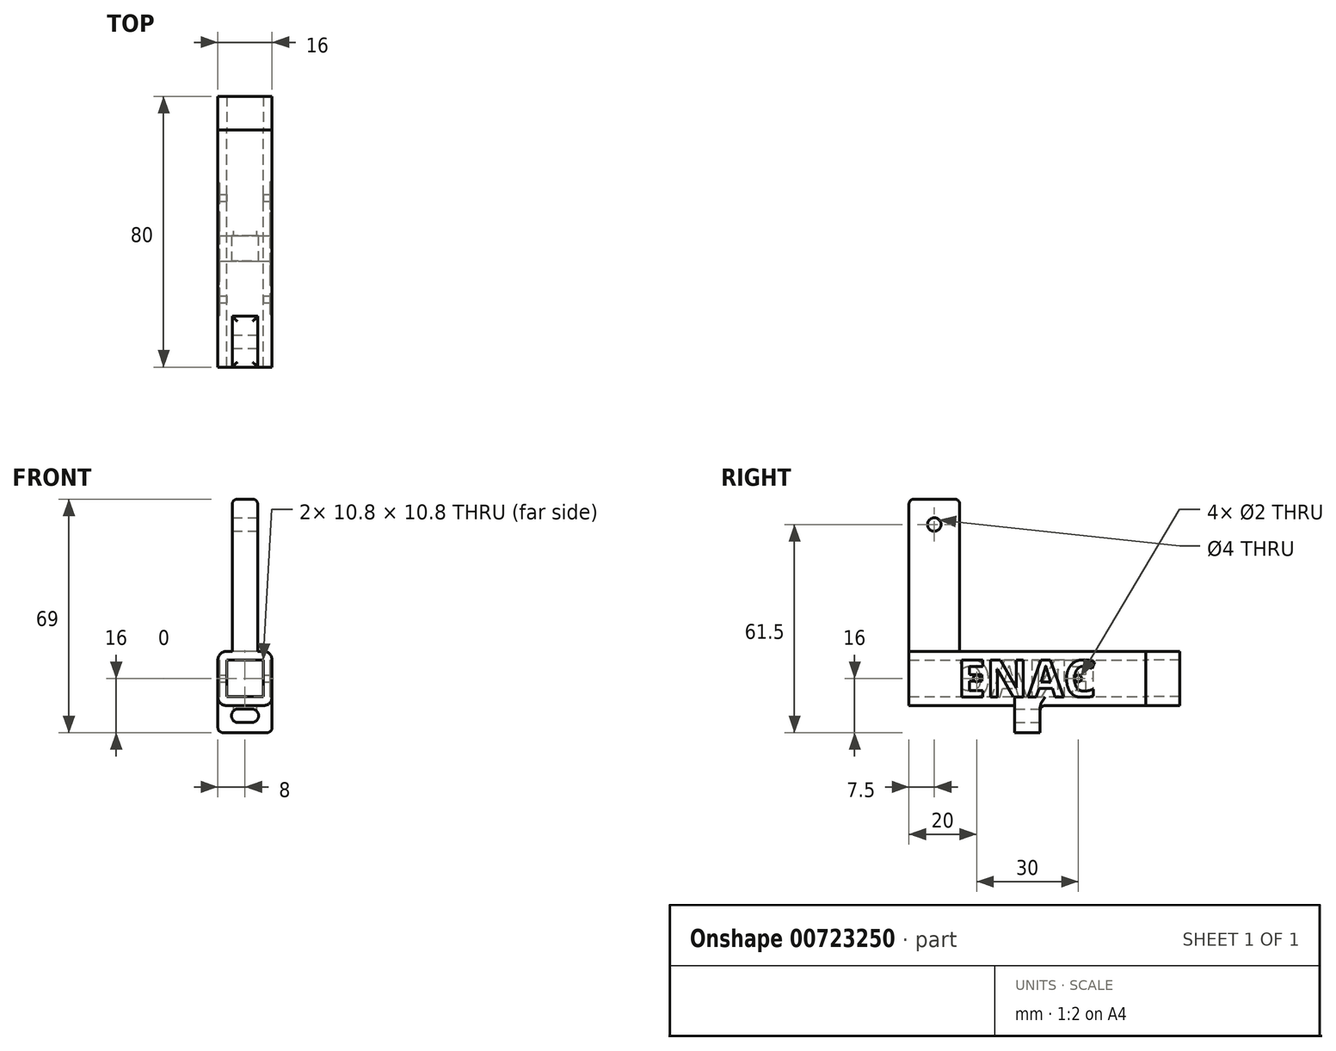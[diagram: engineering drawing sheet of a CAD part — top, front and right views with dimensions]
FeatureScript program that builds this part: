
annotation { "Feature Type Name" : "Feature", "Feature Type Description" : "" }
export const myFeature = defineFeature(function(context is Context, id is Id, definition is map)
    precondition{}
    {
        {
            var Q0;
            Q0=qCreatedBy(makeId("Front.planeOp"),FACE);
            var sketch = newSketch(context, id + "F0", { "sketchPlane" : qUnion([Q0]), "asVersion" : FeatureScriptVersionNumber.V686_LOFT_FS_BUG_FIXES});
            skLineSegment(sketch, "E0.bottom", {"start": v(8, 8) * mm, "end": v(-8, 8) * mm});
            skLineSegment(sketch, "E0.top", {"start": v(8, -8) * mm, "end": v(-8, -8) * mm});
            skLineSegment(sketch, "E0.left", {"start": v(8, 8) * mm, "end": v(8, -8) * mm});
            skLineSegment(sketch, "E0.right", {"start": v(-8, 8) * mm, "end": v(-8, -8) * mm});
            skPoint(sketch, "E0.middle", {"position": v(0, 0) * mm});
            skLineSegment(sketch, "E1.0", {"start": v(5.4, 5.4) * mm, "end": v(-5.4, 5.4) * mm});
            skLineSegment(sketch, "E1.1", {"start": v(5.4, 5.4) * mm, "end": v(5.4, -5.4) * mm});
            skLineSegment(sketch, "E1.2", {"start": v(5.4, -5.4) * mm, "end": v(-5.4, -5.4) * mm});
            skLineSegment(sketch, "E1.3", {"start": v(-5.4, 5.4) * mm, "end": v(-5.4, -5.4) * mm});
            skLineSegment(sketch, "E2.bottom", {"start": v(-8, -8) * mm, "end": v(8, -8) * mm});
            skLineSegment(sketch, "E2.top", {"start": v(-8, -16) * mm, "end": v(8, -16) * mm});
            skLineSegment(sketch, "E2.left", {"start": v(-8, -8) * mm, "end": v(-8, -16) * mm});
            skLineSegment(sketch, "E2.right", {"start": v(8, -8) * mm, "end": v(8, -16) * mm});
            skLineSegment(sketch, "E3", {"start": v(0, -8) * mm, "end": v(0, -16) * mm});
            skLineSegment(sketch, "E4.bottom", {"start": v(4, -9) * mm, "end": v(-4, -9) * mm});
            skLineSegment(sketch, "E4.top", {"start": v(4, -13) * mm, "end": v(-4, -13) * mm});
            skLineSegment(sketch, "E4.left", {"start": v(4, -9) * mm, "end": v(4, -13) * mm});
            skLineSegment(sketch, "E4.right", {"start": v(-4, -9) * mm, "end": v(-4, -13) * mm});
            skPoint(sketch, "E4.middle", {"position": v(0, -11) * mm});
            skSolve(sketch);
        }
        {
            var Q0;
            Q0=makeQuery(id+"F0.imprint","IMPRINT",FACE,{"disambiguationData":[TD([[makeQuery(id+"F0.imprint","IMPRINT",EDGE,{"derivedFrom":sQuery(id+"F0.wireOp",EDGE,"E0.bottom")}),1.0]])]});
            extrude(context, id + "F1", {"entities" : qUnion([Q0]), "endBound" : BoundingType.SYMMETRIC, "depth" : 70 * mm, "offsetDistance" : 25 * mm});
        }
        {
            var Q0;
            {var subQ5=sQuery(id+"F0.wireOp",EDGE,"E2.left");Q0=makeQuery(id+"F0.imprint","IMPRINT",FACE,{"disambiguationData":[TD([[makeQuery(id+"F0.imprint","IMPRINT",EDGE,{"derivedFrom":subQ5}),1.0]])]});}
            var Q1;
            {var subQ0=sQuery(id+"F0.wireOp",EDGE,"E2.right");Q1=makeQuery(id+"F0.imprint","IMPRINT",FACE,{"disambiguationData":[TD([[makeQuery(id+"F0.imprint","IMPRINT",EDGE,{"derivedFrom":subQ0}),-1.0]])]});}
            extrude(context, id + "F2", {"entities" : qUnion([Q0, Q1]), "operationType" : NewBodyOperationType.ADD, "endBound" : BoundingType.SYMMETRIC, "depth" : 7.5 * mm, "offsetDistance" : 25 * mm});
        }
        {
            var Q0;
            Q0=qCreatedBy(makeId("Right.planeOp"),FACE);
            var sketch = newSketch(context, id + "F3", { "sketchPlane" : qUnion([Q0]), "asVersion" : FeatureScriptVersionNumber.V686_LOFT_FS_BUG_FIXES});
            skLineSegment(sketch, "E5.bottom", {"start": v(-35, 8) * mm, "end": v(-20, 8) * mm});
            skLineSegment(sketch, "E5.top", {"start": v(-35, 53) * mm, "end": v(-20, 53) * mm});
            skLineSegment(sketch, "E5.left", {"start": v(-35, 8) * mm, "end": v(-35, 53) * mm});
            skLineSegment(sketch, "E5.right", {"start": v(-20, 8) * mm, "end": v(-20, 53) * mm});
            skPoint(sketch, "E5.middle", {"position": v(-27.5, 45.5) * mm});
            skPoint(sketch, "E6", {"position": v(-15, 0) * mm});
            skPoint(sketch, "E7.MirrorP", {"position": v(15, 0) * mm});
            skLineSegment(sketch, "E8", {"start": v(-35, 53) * mm, "end": v(-35, 38) * mm});
            skLineSegment(sketch, "E9", {"start": v(-35, 38) * mm, "end": v(-20, 38) * mm});
            skLineSegment(sketch, "E10", {"start": v(-20, 38) * mm, "end": v(-20, 53) * mm});
            skSolve(sketch);
        }
        {
            var Q0;
            Q0=makeQuery(id+"F3.imprint","IMPRINT",FACE,{"disambiguationData":[TD([[makeQuery(id+"F3.imprint","IMPRINT",EDGE,{"derivedFrom":sQuery(id+"F3.wireOp",EDGE,"E5.bottom")}),1.0]])]});
            var Q1;
            Q1=makeQuery(id+"F3.imprint","IMPRINT",FACE,{"disambiguationData":[TD([[makeQuery(id+"F3.imprint","IMPRINT",EDGE,{"derivedFrom":sQuery(id+"F3.wireOp",EDGE,"0f00e9bc-2e5d-4239-a3a7-6d6dada13a3e0.MirrorCS")}),1.0]])]});
            var Q2;
            Q2=makeQuery(id+"F3.imprint","IMPRINT",FACE,{"disambiguationData":[TD([[makeQuery(id+"F3.imprint","IMPRINT",EDGE,{"derivedFrom":sQuery(id+"F3.wireOp",EDGE,"E5.top")}),-1.0]])]});
            extrude(context, id + "F4", {"entities" : qUnion([Q0, Q1, Q2]), "operationType" : NewBodyOperationType.ADD, "endBound" : BoundingType.SYMMETRIC, "depth" : 7.5 * mm, "offsetDistance" : 25 * mm});
        }
        {
            var Q0;
            Q0=makeQuery(id+"F4.opExtrude","CAP_FACE",FACE,{"disambiguationData":[OSD([sQuery(id+"F3.wireOp",EDGE,"E5.bottom"),sQuery(id+"F3.wireOp",EDGE,"E5.top"),sQuery(id+"F3.wireOp",EDGE,"E5.left"),sQuery(id+"F3.wireOp",EDGE,"E5.right")])],"isStart":false});
            var sketch = newSketch(context, id + "F5", { "sketchPlane" : qUnion([Q0]), "asVersion" : FeatureScriptVersionNumber.V686_LOFT_FS_BUG_FIXES});
            skPoint(sketch, "E11", {"position": v(-27.5, 45.5) * mm});
            skPoint(sketch, "E12", {"position": v(27.5, 15.5) * mm});
            skSolve(sketch);
        }
        {
            var Q0;
            Q0=makeQuery(id+"F2.boolean.opBoolean","MERGE",FACE,{"derivedFrom":[makeQuery(id+"F1.opExtrude","SWEPT_FACE",FACE,{"disambiguationData":[OSD([sQuery(id+"F0.wireOp",EDGE,"E0.left")])]}),makeQuery(id+"F2.opExtrude","SWEPT_FACE",FACE,{"disambiguationData":[OSD([sQuery(id+"F0.wireOp",EDGE,"E2.right")])]})]});
            var sketch = newSketch(context, id + "F6", { "sketchPlane" : qUnion([Q0]), "asVersion" : FeatureScriptVersionNumber.V686_LOFT_FS_BUG_FIXES});
            skPoint(sketch, "E13", {"position": v(-15, 0) * mm});
            skPoint(sketch, "E14", {"position": v(15, 0) * mm});
            skSolve(sketch);
        }
        {
            var Q0;
            Q0=sQuery(id+"F5.wireOp",VERTEX,"E11");
            var Q1;
            Q1=sQuery(id+"F5.wireOp",VERTEX,"E12");
            var Q2;
            Q2=makeQuery(id+"F1.opExtrude","SWEPT_BODY",BODY,{"disambiguationData":[OSD([sQuery(id+"F0.wireOp",EDGE,"E0.bottom"),sQuery(id+"F0.wireOp",EDGE,"E0.left"),sQuery(id+"F0.wireOp",EDGE,"E0.right"),sQuery(id+"F0.wireOp",EDGE,"E1.0"),sQuery(id+"F0.wireOp",EDGE,"E1.1"),sQuery(id+"F0.wireOp",EDGE,"E1.2"),sQuery(id+"F0.wireOp",EDGE,"E1.3"),sQuery(id+"F0.wireOp",EDGE,"E2.bottom")])]});
            hole(context, id + "F7", {"style" : HoleStyle.SIMPLE, "endStyle" : HoleEndStyle.THROUGH, "holeDiameter" : 4 * mm, "majorDiameter" : 5 * mm, "isTappedThrough" : true, "tappedDepth" : 12 * mm, "tapClearance" : 3, "locations" : qUnion([Q0, Q1]), "scope" : qUnion([Q2])});
        }
        {
            var Q0;
            Q0=sQuery(id+"F6.wireOp",VERTEX,"E13");
            var Q1;
            Q1=sQuery(id+"F6.wireOp",VERTEX,"9b55d32a-54b2-4053-a118-dd1e83ebf03c0.MirrorP");
            var Q2;
            Q2=sQuery(id+"F6.wireOp",VERTEX,"E14");
            var Q3;
            Q3=makeQuery(id+"F1.opExtrude","SWEPT_BODY",BODY,{"disambiguationData":[OSD([sQuery(id+"F0.wireOp",EDGE,"E0.bottom"),sQuery(id+"F0.wireOp",EDGE,"E0.left"),sQuery(id+"F0.wireOp",EDGE,"E0.right"),sQuery(id+"F0.wireOp",EDGE,"E1.0"),sQuery(id+"F0.wireOp",EDGE,"E1.1"),sQuery(id+"F0.wireOp",EDGE,"E1.2"),sQuery(id+"F0.wireOp",EDGE,"E1.3"),sQuery(id+"F0.wireOp",EDGE,"E2.bottom")])]});
            hole(context, id + "F8", {"style" : HoleStyle.SIMPLE, "endStyle" : HoleEndStyle.THROUGH, "holeDiameter" : 2 * mm, "majorDiameter" : 5 * mm, "isTappedThrough" : true, "tappedDepth" : 12 * mm, "tapClearance" : 3, "locations" : qUnion([Q0, Q1, Q2]), "scope" : qUnion([Q3])});
        }
        {
            var Q0;
            {var subQ0=sQuery(id+"F0.wireOp",EDGE,"E2.left");var subQ1=sQuery(id+"F0.wireOp",EDGE,"E2.bottom");var subQ2=sQuery(id+"F0.wireOp",EDGE,"E0.right");Q0=makeQuery(id+"F2.boolean.opBoolean","SPLIT",EDGE,{"disambiguationData":[TD([makeQuery(id+"F1.opExtrude","CAP_FACE",FACE,{"disambiguationData":[OSD([sQuery(id+"F0.wireOp",EDGE,"E0.bottom"),sQuery(id+"F0.wireOp",EDGE,"E0.left"),subQ2,sQuery(id+"F0.wireOp",EDGE,"E1.0"),sQuery(id+"F0.wireOp",EDGE,"E1.1"),sQuery(id+"F0.wireOp",EDGE,"E1.2"),sQuery(id+"F0.wireOp",EDGE,"E1.3"),subQ1])],"isStart":false})])],"derivedFrom":makeQuery(id+"F1.opExtrude","SWEPT_EDGE",EDGE,{"disambiguationData":[OSD([subQ2,subQ1,subQ0])]})});}
            var Q1;
            Q1=makeQuery(id+"F1.opExtrude","SWEPT_EDGE",EDGE,{"disambiguationData":[OSD([sQuery(id+"F0.wireOp",EDGE,"E0.bottom"),sQuery(id+"F0.wireOp",EDGE,"E0.right")])]});
            var Q2;
            {var subQ0=sQuery(id+"F0.wireOp",EDGE,"E2.left");var subQ1=sQuery(id+"F0.wireOp",EDGE,"E2.bottom");var subQ2=sQuery(id+"F0.wireOp",EDGE,"E0.right");Q2=makeQuery(id+"F2.boolean.opBoolean","SPLIT",EDGE,{"disambiguationData":[TD([makeQuery(id+"F1.opExtrude","CAP_FACE",FACE,{"disambiguationData":[OSD([sQuery(id+"F0.wireOp",EDGE,"E0.bottom"),sQuery(id+"F0.wireOp",EDGE,"E0.left"),subQ2,sQuery(id+"F0.wireOp",EDGE,"E1.0"),sQuery(id+"F0.wireOp",EDGE,"E1.1"),sQuery(id+"F0.wireOp",EDGE,"E1.2"),sQuery(id+"F0.wireOp",EDGE,"E1.3"),subQ1])],"isStart":true})])],"derivedFrom":makeQuery(id+"F1.opExtrude","SWEPT_EDGE",EDGE,{"disambiguationData":[OSD([subQ2,subQ1,subQ0])]})});}
            var Q3;
            Q3=makeQuery(id+"F1.opExtrude","SWEPT_EDGE",EDGE,{"disambiguationData":[OSD([sQuery(id+"F0.wireOp",EDGE,"E0.bottom"),sQuery(id+"F0.wireOp",EDGE,"E0.left")])]});
            var Q4;
            {var subQ0=sQuery(id+"F0.wireOp",EDGE,"E2.bottom");var subQ1=sQuery(id+"F0.wireOp",EDGE,"E2.right");var subQ2=sQuery(id+"F0.wireOp",EDGE,"E0.left");Q4=makeQuery(id+"F2.boolean.opBoolean","SPLIT",EDGE,{"disambiguationData":[TD([makeQuery(id+"F1.opExtrude","CAP_FACE",FACE,{"disambiguationData":[OSD([sQuery(id+"F0.wireOp",EDGE,"E0.bottom"),subQ2,sQuery(id+"F0.wireOp",EDGE,"E0.right"),sQuery(id+"F0.wireOp",EDGE,"E1.0"),sQuery(id+"F0.wireOp",EDGE,"E1.1"),sQuery(id+"F0.wireOp",EDGE,"E1.2"),sQuery(id+"F0.wireOp",EDGE,"E1.3"),subQ0])],"isStart":false})])],"derivedFrom":makeQuery(id+"F1.opExtrude","SWEPT_EDGE",EDGE,{"disambiguationData":[OSD([subQ2,subQ0,subQ1])]})});}
            var Q5;
            {var subQ0=sQuery(id+"F0.wireOp",EDGE,"E2.right");var subQ1=sQuery(id+"F0.wireOp",EDGE,"E2.bottom");var subQ2=sQuery(id+"F0.wireOp",EDGE,"E0.left");Q5=makeQuery(id+"F2.boolean.opBoolean","SPLIT",EDGE,{"disambiguationData":[TD([makeQuery(id+"F1.opExtrude","CAP_FACE",FACE,{"disambiguationData":[OSD([sQuery(id+"F0.wireOp",EDGE,"E0.bottom"),subQ2,sQuery(id+"F0.wireOp",EDGE,"E0.right"),sQuery(id+"F0.wireOp",EDGE,"E1.0"),sQuery(id+"F0.wireOp",EDGE,"E1.1"),sQuery(id+"F0.wireOp",EDGE,"E1.2"),sQuery(id+"F0.wireOp",EDGE,"E1.3"),subQ1])],"isStart":true})])],"derivedFrom":makeQuery(id+"F1.opExtrude","SWEPT_EDGE",EDGE,{"disambiguationData":[OSD([subQ2,subQ1,subQ0])]})});}
            fillet(context, id + "F9", {"entities" : qUnion([Q0, Q1, Q2, Q3, Q4, Q5]), "radius" : 2.5 * mm, "tangentPropagation" : true, "allowEdgeOverflow" : false});
        }
        {
            var Q0;
            Q0=makeQuery(id+"F2.opExtrude","SWEPT_EDGE",EDGE,{"disambiguationData":[OSD([sQuery(id+"F0.wireOp",EDGE,"E4.bottom"),sQuery(id+"F0.wireOp",EDGE,"E4.right")])]});
            var Q1;
            Q1=makeQuery(id+"F2.opExtrude","SWEPT_EDGE",EDGE,{"disambiguationData":[OSD([sQuery(id+"F0.wireOp",EDGE,"E4.bottom"),sQuery(id+"F0.wireOp",EDGE,"E4.left")])]});
            var Q2;
            Q2=makeQuery(id+"F2.opExtrude","SWEPT_EDGE",EDGE,{"disambiguationData":[OSD([sQuery(id+"F0.wireOp",EDGE,"E4.top"),sQuery(id+"F0.wireOp",EDGE,"E4.left")])]});
            var Q3;
            Q3=makeQuery(id+"F2.opExtrude","SWEPT_EDGE",EDGE,{"disambiguationData":[OSD([sQuery(id+"F0.wireOp",EDGE,"E4.top"),sQuery(id+"F0.wireOp",EDGE,"E4.right")])]});
            fillet(context, id + "F10", {"entities" : qUnion([Q0, Q1, Q2, Q3]), "radius" : 2 * mm, "tangentPropagation" : true, "allowEdgeOverflow" : false});
        }
        {
            var Q0;
            Q0=makeQuery(id+"F4.opExtrude","SWEPT_EDGE",EDGE,{"disambiguationData":[OSD([sQuery(id+"F3.wireOp",EDGE,"E5.top"),sQuery(id+"F3.wireOp",EDGE,"E5.left")])]});
            var Q1;
            Q1=makeQuery(id+"F4.opExtrude","CAP_EDGE",EDGE,{"disambiguationData":[OSD([sQuery(id+"F3.wireOp",EDGE,"E5.top")])],"isStart":true});
            var Q2;
            Q2=makeQuery(id+"F4.opExtrude","CAP_EDGE",EDGE,{"disambiguationData":[OSD([sQuery(id+"F3.wireOp",EDGE,"E5.top")])],"isStart":false});
            var Q3;
            Q3=makeQuery(id+"F4.opExtrude","SWEPT_EDGE",EDGE,{"disambiguationData":[OSD([sQuery(id+"F3.wireOp",EDGE,"E5.top"),sQuery(id+"F3.wireOp",EDGE,"E5.right")])]});
            var Q4;
            Q4=makeQuery(id+"F4.opExtrude","SWEPT_EDGE",EDGE,{"disambiguationData":[OSD([sQuery(id+"F3.wireOp",EDGE,"E5.bottom"),sQuery(id+"F3.wireOp",EDGE,"E5.right")])]});
            var Q5;
            Q5=makeQuery(id+"F4.opExtrude","SWEPT_EDGE",EDGE,{"disambiguationData":[OSD([sQuery(id+"F3.wireOp",EDGE,"0f00e9bc-2e5d-4239-a3a7-6d6dada13a3e0.MirrorCS"),sQuery(id+"F3.wireOp",EDGE,"26c6a95d-d3fd-4abb-9b3b-3dd4256fe6a70.MirrorCS")])]});
            var Q6;
            Q6=makeQuery(id+"F4.opExtrude","CAP_EDGE",EDGE,{"disambiguationData":[OSD([sQuery(id+"F3.wireOp",EDGE,"0f00e9bc-2e5d-4239-a3a7-6d6dada13a3e0.MirrorCS")])],"isStart":true});
            var Q7;
            Q7=makeQuery(id+"F4.opExtrude","CAP_EDGE",EDGE,{"disambiguationData":[OSD([sQuery(id+"F3.wireOp",EDGE,"0f00e9bc-2e5d-4239-a3a7-6d6dada13a3e0.MirrorCS")])],"isStart":false});
            var Q8;
            Q8=makeQuery(id+"F4.opExtrude","SWEPT_EDGE",EDGE,{"disambiguationData":[OSD([sQuery(id+"F3.wireOp",EDGE,"0f00e9bc-2e5d-4239-a3a7-6d6dada13a3e0.MirrorCS"),sQuery(id+"F3.wireOp",EDGE,"606600f1-0bf8-45a2-96d5-3932373f95270.MirrorCS")])]});
            var Q9;
            Q9=makeQuery(id+"F4.opExtrude","SWEPT_EDGE",EDGE,{"disambiguationData":[OSD([sQuery(id+"F3.wireOp",EDGE,"26c6a95d-d3fd-4abb-9b3b-3dd4256fe6a70.MirrorCS"),sQuery(id+"F3.wireOp",EDGE,"b672d35b-5d45-4f97-80e9-863e662cdbea0.MirrorCS")])]});
            var Q10;
            Q10=makeQuery(id+"F2.opExtrude","SWEPT_EDGE",EDGE,{"disambiguationData":[OSD([sQuery(id+"F0.wireOp",EDGE,"E2.top"),sQuery(id+"F0.wireOp",EDGE,"E2.right")])]});
            var Q11;
            Q11=makeQuery(id+"F2.opExtrude","SWEPT_EDGE",EDGE,{"disambiguationData":[OSD([sQuery(id+"F0.wireOp",EDGE,"E2.top"),sQuery(id+"F0.wireOp",EDGE,"E2.left")])]});
            var Q12;
            Q12=makeQuery(id+"F2.opExtrude","CAP_EDGE",EDGE,{"disambiguationData":[OSD([sQuery(id+"F0.wireOp",EDGE,"E2.bottom")])],"isStart":false});
            var Q13;
            Q13=makeQuery(id+"F2.opExtrude","CAP_EDGE",EDGE,{"disambiguationData":[OSD([sQuery(id+"F0.wireOp",EDGE,"E2.bottom")])],"isStart":true});
            fillet(context, id + "F11", {"entities" : qUnion([Q0, Q1, Q2, Q3, Q4, Q5, Q6, Q7, Q8, Q9, Q10, Q11, Q12, Q13]), "radius" : 1.5 * mm, "tangentPropagation" : true, "allowEdgeOverflow" : false});
        }
        {
            var Q0;
            Q0=makeQuery(id+"F2.boolean.opBoolean","MERGE",FACE,{"derivedFrom":[makeQuery(id+"F1.opExtrude","SWEPT_FACE",FACE,{"disambiguationData":[OSD([sQuery(id+"F0.wireOp",EDGE,"E0.left")])]}),makeQuery(id+"F2.opExtrude","SWEPT_FACE",FACE,{"disambiguationData":[OSD([sQuery(id+"F0.wireOp",EDGE,"E2.right")])]})]});
            var sketch = newSketch(context, id + "F12", { "sketchPlane" : qUnion([Q0]), "asVersion" : FeatureScriptVersionNumber.V686_LOFT_FS_BUG_FIXES});
            skText(sketch, "E15", { "text": "ENAC", "fontName": "OpenSans-Bold.ttf"});
            const initialGuessF12  = {"E15": [-0.02085, -0.0055, 1, 0, 0.011]};
            skSetInitialGuess(sketch, initialGuessF12);
            skSolve(sketch);
        }
        {
            var Q0;
            Q0=makeQuery(id+"F2.boolean.opBoolean","MERGE",FACE,{"derivedFrom":[makeQuery(id+"F1.opExtrude","SWEPT_FACE",FACE,{"disambiguationData":[OSD([sQuery(id+"F0.wireOp",EDGE,"E0.right")])]}),makeQuery(id+"F2.opExtrude","SWEPT_FACE",FACE,{"disambiguationData":[OSD([sQuery(id+"F0.wireOp",EDGE,"E2.left")])]})]});
            var sketch = newSketch(context, id + "F13", { "sketchPlane" : qUnion([Q0]), "asVersion" : FeatureScriptVersionNumber.V686_LOFT_FS_BUG_FIXES});
            skText(sketch, "E16", { "text": "ENAC", "fontName": "OpenSans-Bold.ttf"});
            const initialGuessF13  = {"E16": [-0.02085, -0.0055, 1, 0, 0.011]};
            skSetInitialGuess(sketch, initialGuessF13);
            skSolve(sketch);
        }
        {
            var Q0;
            Q0=makeQuery(id+"F12.imprint","IMPRINT",FACE,{"disambiguationData":[TD([[makeQuery(id+"F12.imprint","IMPRINT",EDGE,{"derivedFrom":sQuery(id+"F12.wireOp",EDGE,"E15.sketch_text.stroke-0")}),1.0]])]});
            var Q1;
            Q1=makeQuery(id+"F12.imprint","IMPRINT",FACE,{"disambiguationData":[TD([[makeQuery(id+"F12.imprint","IMPRINT",EDGE,{"derivedFrom":sQuery(id+"F12.wireOp",EDGE,"E15.sketch_text.stroke-12")}),-1.0]])]});
            var Q2;
            Q2=makeQuery(id+"F12.imprint","IMPRINT",FACE,{"disambiguationData":[TD([[makeQuery(id+"F12.imprint","IMPRINT",EDGE,{"derivedFrom":sQuery(id+"F12.wireOp",EDGE,"E15.sketch_text.stroke-26")}),-1.0]])]});
            var Q3;
            Q3=makeQuery(id+"F12.imprint","IMPRINT",FACE,{"disambiguationData":[TD([[makeQuery(id+"F12.imprint","IMPRINT",EDGE,{"derivedFrom":sQuery(id+"F12.wireOp",EDGE,"E15.sketch_text.stroke-38")}),-1.0]])]});
            extrude(context, id + "F14", {"entities" : qUnion([Q0, Q1, Q2, Q3]), "operationType" : NewBodyOperationType.REMOVE, "oppositeDirection" : true, "depth" : 0.5 * mm, "offsetDistance" : 25 * mm});
        }
        {
            var Q0;
            Q0=makeQuery(id+"F13.imprint","IMPRINT",FACE,{"disambiguationData":[TD([[makeQuery(id+"F13.imprint","IMPRINT",EDGE,{"derivedFrom":sQuery(id+"F13.wireOp",EDGE,"E16.sketch_text.stroke-0")}),1.0]])]});
            var Q1;
            Q1=makeQuery(id+"F13.imprint","IMPRINT",FACE,{"disambiguationData":[TD([[makeQuery(id+"F13.imprint","IMPRINT",EDGE,{"derivedFrom":sQuery(id+"F13.wireOp",EDGE,"E16.sketch_text.stroke-12")}),-1.0]])]});
            var Q2;
            Q2=makeQuery(id+"F13.imprint","IMPRINT",FACE,{"disambiguationData":[TD([[makeQuery(id+"F13.imprint","IMPRINT",EDGE,{"derivedFrom":sQuery(id+"F13.wireOp",EDGE,"E16.sketch_text.stroke-26")}),-1.0]])]});
            var Q3;
            Q3=makeQuery(id+"F13.imprint","IMPRINT",FACE,{"disambiguationData":[TD([[makeQuery(id+"F13.imprint","IMPRINT",EDGE,{"derivedFrom":sQuery(id+"F13.wireOp",EDGE,"E16.sketch_text.stroke-38")}),-1.0]])]});
            extrude(context, id + "F15", {"entities" : qUnion([Q0, Q1, Q2, Q3]), "operationType" : NewBodyOperationType.REMOVE, "oppositeDirection" : true, "depth" : .5 * mm, "offsetDistance" : 25 * mm});
        }
        {
            var Q0;
            Q0=makeQuery(id+"F1.opExtrude","CAP_FACE",FACE,{"disambiguationData":[OSD([sQuery(id+"F0.wireOp",EDGE,"E0.bottom"),sQuery(id+"F0.wireOp",EDGE,"E0.left"),sQuery(id+"F0.wireOp",EDGE,"E0.right"),sQuery(id+"F0.wireOp",EDGE,"E1.0"),sQuery(id+"F0.wireOp",EDGE,"E1.1"),sQuery(id+"F0.wireOp",EDGE,"E1.2"),sQuery(id+"F0.wireOp",EDGE,"E1.3"),sQuery(id+"F0.wireOp",EDGE,"E2.bottom")])],"isStart":true});
            extrude(context, id + "F16", {"entities" : qUnion([Q0]), "depth" : 10 * mm, "offsetDistance" : 25 * mm});
        }
    });
